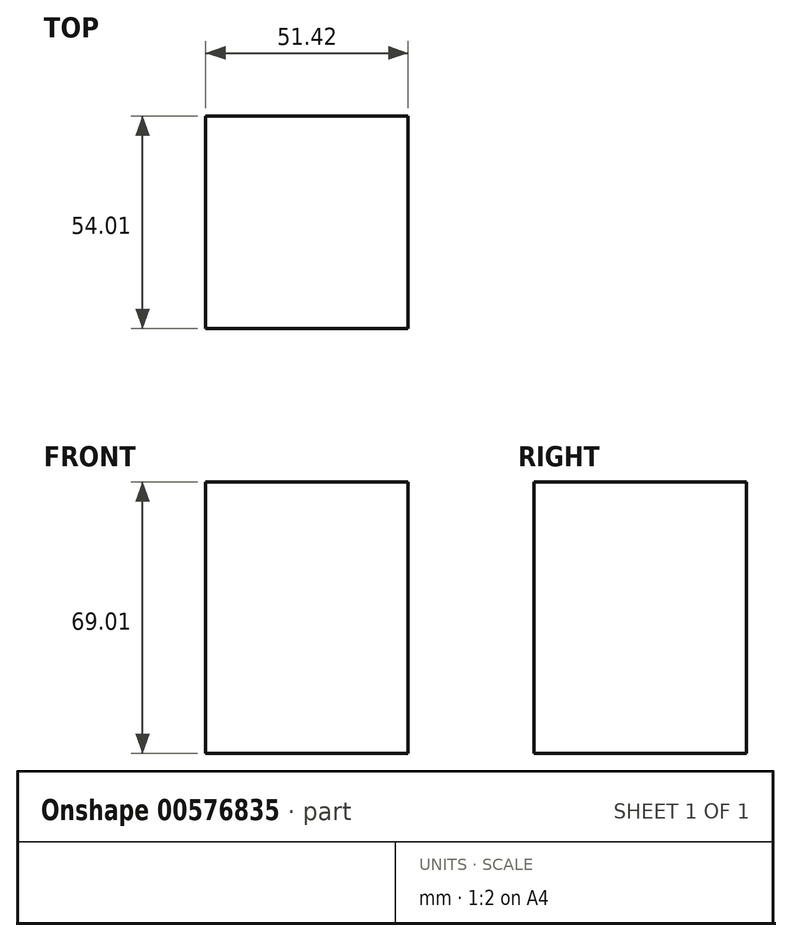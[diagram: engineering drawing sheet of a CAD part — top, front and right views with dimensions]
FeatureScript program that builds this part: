
annotation { "Feature Type Name" : "Feature", "Feature Type Description" : "" }
export const myFeature = defineFeature(function(context is Context, id is Id, definition is map)
    precondition{}
    {
        {
            var Q0;
            Q0=qCreatedBy(makeId("Top.planeOp"),FACE);
            var sketch = newSketch(context, id + "F0", { "sketchPlane" : qUnion([Q0])});
            skLineSegment(sketch, "E0", {"start": v(0, 79.71) * mm, "end": v(-26.42, 79.71) * mm});
            skLineSegment(sketch, "E1", {"start": v(-26.42, 79.71) * mm, "end": v(0, 79.71) * mm, "construction": true});
            skSolve(sketch);
        }
        {
            var Q0;
            Q0=sQuery(id+"F0.wireOp",EDGE,"E0");
            extrude(context, id + "F1", {"bodyType" : ToolBodyType.SURFACE, "surfaceEntities" : qUnion([Q0]), "depth" : 14.95 * mm, "offsetDistance" : 25 * mm});
        }
        {
            var Q0;
            Q0=makeQuery(id+"F1.opExtrude","SWEPT_FACE",FACE,{"disambiguationData":[OSD([sQuery(id+"F0.wireOp",EDGE,"E0")])]});
            extrude(context, id + "F2", {"entities" : qUnion([Q0]), "depth" : 54 * mm, "offsetDistance" : 25 * mm});
        }
        {
            var Q0;
            {var subQ0=sQuery(id+"F0.wireOp",EDGE,"E0");Q0=makeQuery(id+"F2.opExtrude","SWEPT_FACE",FACE,{"disambiguationData":[OSD([subQ0]),TDD([makeQuery(id+"F1.opExtrude","CAP_EDGE",EDGE,{"disambiguationData":[OSD([subQ0])],"isStart":true})])]});}
            var sketch = newSketch(context, id + "F3", { "sketchPlane" : qUnion([Q0])});
            skSolve(sketch);
        }
        {
            var Q0;
            {var subQ0=sQuery(id+"F0.wireOp",VERTEX,"E0.start");Q0=makeQuery(id+"F3.imprint","IMPRINT",FACE,{"disambiguationData":[TD([[makeQuery(id+"F3.imprint","IMPRINT",EDGE,{"derivedFrom":makeQuery(id+"F2.opExtrude","SWEPT_EDGE",EDGE,{"disambiguationData":[OSD([subQ0]),TDD([makeQuery(id+"F1.opExtrude","CAP_VERTEX",VERTEX,{"disambiguationData":[OSD([subQ0])],"isStart":true})])]})}),1.0]])]});}
            extrude(context, id + "F4", {"entities" : qUnion([Q0]), "operationType" : NewBodyOperationType.ADD, "depth" : 54.06 * mm, "offsetDistance" : 25 * mm});
        }
        {
            var Q0;
            {var subQ0=sQuery(id+"F0.wireOp",VERTEX,"E0.end");Q0=makeQuery(id+"F4.boolean.opBoolean","MERGE",FACE,{"derivedFrom":[makeQuery(id+"F2.opExtrude","SWEPT_FACE",FACE,{"disambiguationData":[OSD([subQ0])]}),makeQuery(id+"F4.opExtrude","SWEPT_FACE",FACE,{"disambiguationData":[OSD([subQ0])]})]});}
            extrude(context, id + "F5", {"entities" : qUnion([Q0]), "operationType" : NewBodyOperationType.ADD, "depth" : 25 * mm, "offsetDistance" : 25 * mm});
        }
    });
